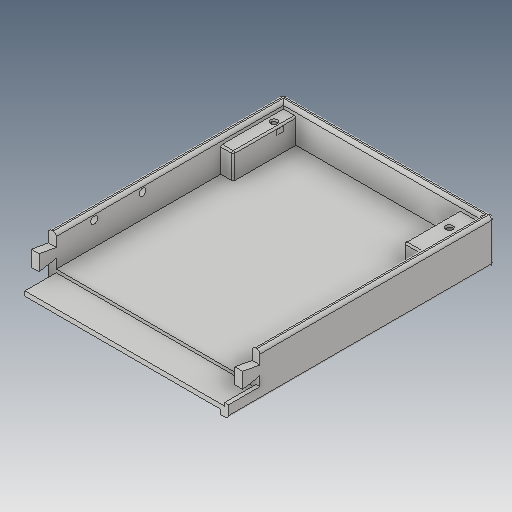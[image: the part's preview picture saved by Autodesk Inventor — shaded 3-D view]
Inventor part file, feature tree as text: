
AUTODESK INVENTOR PART (.ipt)
format: ipt  version: 2019 (Build 230136000, 136)  size: 365,056 bytes
history: native  units: mm
features: extrude x7, sketch x7, other x5, fillet x2, projected_geometry x2, surface_op x1, plane x1
ambient origin geometry x8: Origin, YZ Plane, XZ Plane, XY Plane, X Axis, Y Axis, Z Axis, Center Point
bodies: Solid1 (feature_tree)
feature tree (25):
  extrude  "Extrusion1"  Depth=170.0mm
  extrude  "Extrusion2"  Depth=5.0mm
  extrude  "Extrusion3"  Depth=25.0mm TaperAngle=0.0deg
  fillet  "Fillet1"  Radius=2.0mm
  surface_op  "Sculpt2"
  extrude  "Extrusion4"  TaperAngle=0.0deg  [1 undecoded]
  extrude  "Extrusion5"  Depth=40.0mm
  fillet  "Fillet2"  [1 undecoded]
  extrude  "Extrusion7"  Depth=35.0mm
  plane  "Work Plane1"
  extrude  "Extrusion8"  Depth=16.0mm TaperAngle=0.0deg
  sketch  "Sketch1"  dims[d0=135.0mm d1=170.0mm]
  sketch  "Sketch2"  dims[d2=28.0mm d3=0.0mm d4=5.0mm]
  projected_geometry  "Projected Loop1"
  sketch  "Sketch3"  dims[d5=20.0mm d6=0.0mm d7=25.0mm d8=0.0mm d9=2.0mm]
  projected_geometry  "Projected Loop2"
  sketch  "Sketch4"  dims[d10=0.0mm d11=0.0mm]
  sketch  "Sketch5"  dims[d12=8.0mm d13=40.0mm d14=0.0mm]
  sketch  "Sketch6"  dims[d15=0.0mm d16=35.0mm]
  sketch  "Sketch7"  dims[d17=13.0mm d18=16.0mm d19=0.0mm d20=4.5mm d22=4.0mm d23=4.5mm d24=6.5mm d26=12.0mm d27=0.0mm d28=1.0mm d29=4.5mm d30=4.5mm d31=30.8mm d32=5.0mm d34=90.0mm d37=0.0mm d38=0.0mm d39=-1.5mm d40=7.5mm d41=7.5mm d42=3.15mm d43=0.0mm d44=10.0mm d45=12.5mm]
  other  "Composite2"
  other  "Srf2"
  parser-record x1  (decoder bookkeeping rows leaked as tree rows — omitted from the tree; the rows remain in map.json)
  other  "CaseA.iam"
  other  "Case_A1:1"
note: 2 required parameter values undecoded (feature->parameter linkage not recoverable at this tier; creation-order binding heuristic only, values carry confidence <= 0.55)
note: 1 file-system path scrubbed to <path> (originals preserved in map.json)
